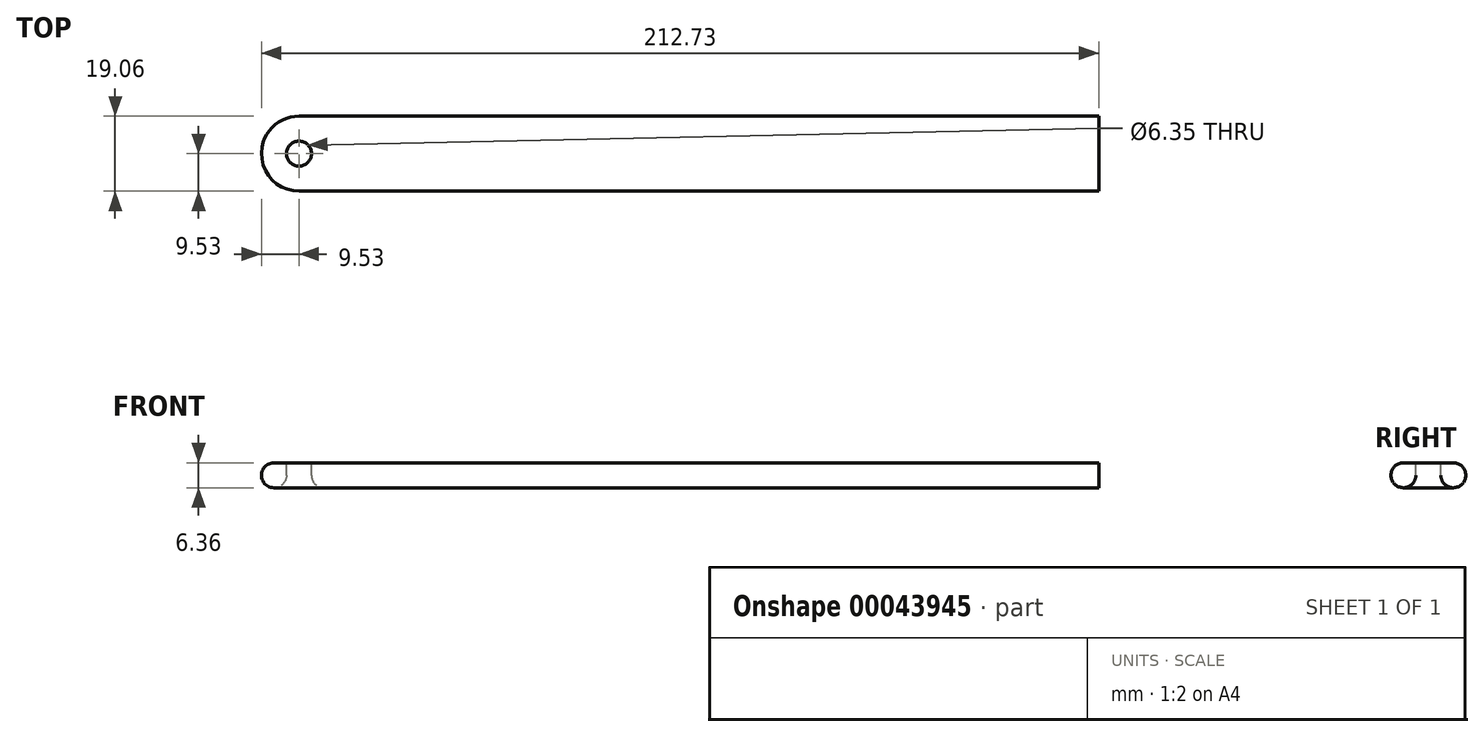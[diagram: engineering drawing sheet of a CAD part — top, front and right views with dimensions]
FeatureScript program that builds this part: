
annotation { "Feature Type Name" : "Feature", "Feature Type Description" : "" }
export const myFeature = defineFeature(function(context is Context, id is Id, definition is map)
    precondition{}
    {
        {
            var Q0;
            Q0=qCreatedBy(makeId("Top.planeOp"),FACE);
            var sketch = newSketch(context, id + "F0", { "sketchPlane" : qUnion([Q0])});
            skLineSegment(sketch, "E0.rect.bottom", {"start": v(101.6, 9.53) * mm, "end": v(-101.6, 9.53) * mm});
            skLineSegment(sketch, "E0.rect.top", {"start": v(101.6, -9.52) * mm, "end": v(-101.6, -9.52) * mm});
            skLineSegment(sketch, "E0.rect.left", {"start": v(101.6, 9.53) * mm, "end": v(101.6, -9.52) * mm});
            skPoint(sketch, "E0.rect.middle", {"position": v(0, 0) * mm});
            skArc(sketch, "E1", {"start": v(-101.6, 9.53) * mm, "mid": v(-111.13, 0) * mm, "end": v(-101.6, -9.52) * mm});
            skSolve(sketch);
        }
        {
            var Q0;
            Q0 = qSketchRegion(id + "F0", true);
            extrude(context, id + "F1", {"entities" : qUnion([Q0]), "endBound" : BoundingType.SYMMETRIC, "depth" : 6.35 * mm});
        }
        {
            var Q0;
            Q0=makeQuery(id+"F1.opExtrude","CAP_FACE",FACE,{"disambiguationData":[OSD([sQuery(id+"F0.wireOp",EDGE,"E0.rect.bottom"),sQuery(id+"F0.wireOp",EDGE,"E0.rect.top"),sQuery(id+"F0.wireOp",EDGE,"E0.rect.left"),sQuery(id+"F0.wireOp",EDGE,"E1")])],"isStart":false});
            var sketch = newSketch(context, id + "F2", { "sketchPlane" : qUnion([Q0])});
            skCircle(sketch, "E2", {"center": v(-101.6, 0) * mm, "radius": 3.18 * mm});
            skSolve(sketch);
        }
        {
            var Q0;
            Q0 = qSketchRegion(id + "F2", true);
            extrude(context, id + "F3", {"entities" : qUnion([Q0]), "operationType" : NewBodyOperationType.REMOVE, "endBound" : BoundingType.THROUGH_ALL, "oppositeDirection" : true, "depth" : 25.4 * mm});
        }
        {
            var Q0;
            Q0=makeQuery(id+"F1.opExtrude","CAP_EDGE",EDGE,{"disambiguationData":[OSD([sQuery(id+"F0.wireOp",EDGE,"E0.rect.top")])],"isStart":false});
            var Q1;
            Q1=makeQuery(id+"F3.boolean.opBoolean","COPY",EDGE,{"derivedFrom":makeQuery(id+"F3.opExtrude","CAP_EDGE",EDGE,{"disambiguationData":[OSD([sQuery(id+"F2.wireOp",EDGE,"E2")])],"isStart":true})});
            fillet(context, id + "F4", {"entities" : qUnion([Q0, Q1]), "radius" : 3.17 * mm, "tangentPropagation" : true, "allowEdgeOverflow" : false});
        }
        {
            var Q0;
            Q0=makeQuery(id+"F1.opExtrude","CAP_EDGE",EDGE,{"disambiguationData":[OSD([sQuery(id+"F0.wireOp",EDGE,"E0.rect.top")])],"isStart":true});
            var Q1;
            Q1=makeQuery(id+"F3.boolean.opBoolean","INTERSECT",EDGE,{"derivedFrom":[makeQuery(id+"F1.opExtrude","CAP_FACE",FACE,{"disambiguationData":[OSD([sQuery(id+"F0.wireOp",EDGE,"E0.rect.bottom"),sQuery(id+"F0.wireOp",EDGE,"E0.rect.top"),sQuery(id+"F0.wireOp",EDGE,"E0.rect.left"),sQuery(id+"F0.wireOp",EDGE,"E1")])],"isStart":true}),makeQuery(id+"F3.opExtrude","SWEPT_FACE",FACE,{"disambiguationData":[OSD([sQuery(id+"F2.wireOp",EDGE,"E2")])]})]});
            fillet(context, id + "F5", {"entities" : qUnion([Q0, Q1]), "radius" : 3.17 * mm, "tangentPropagation" : true, "allowEdgeOverflow" : false});
        }
    });
